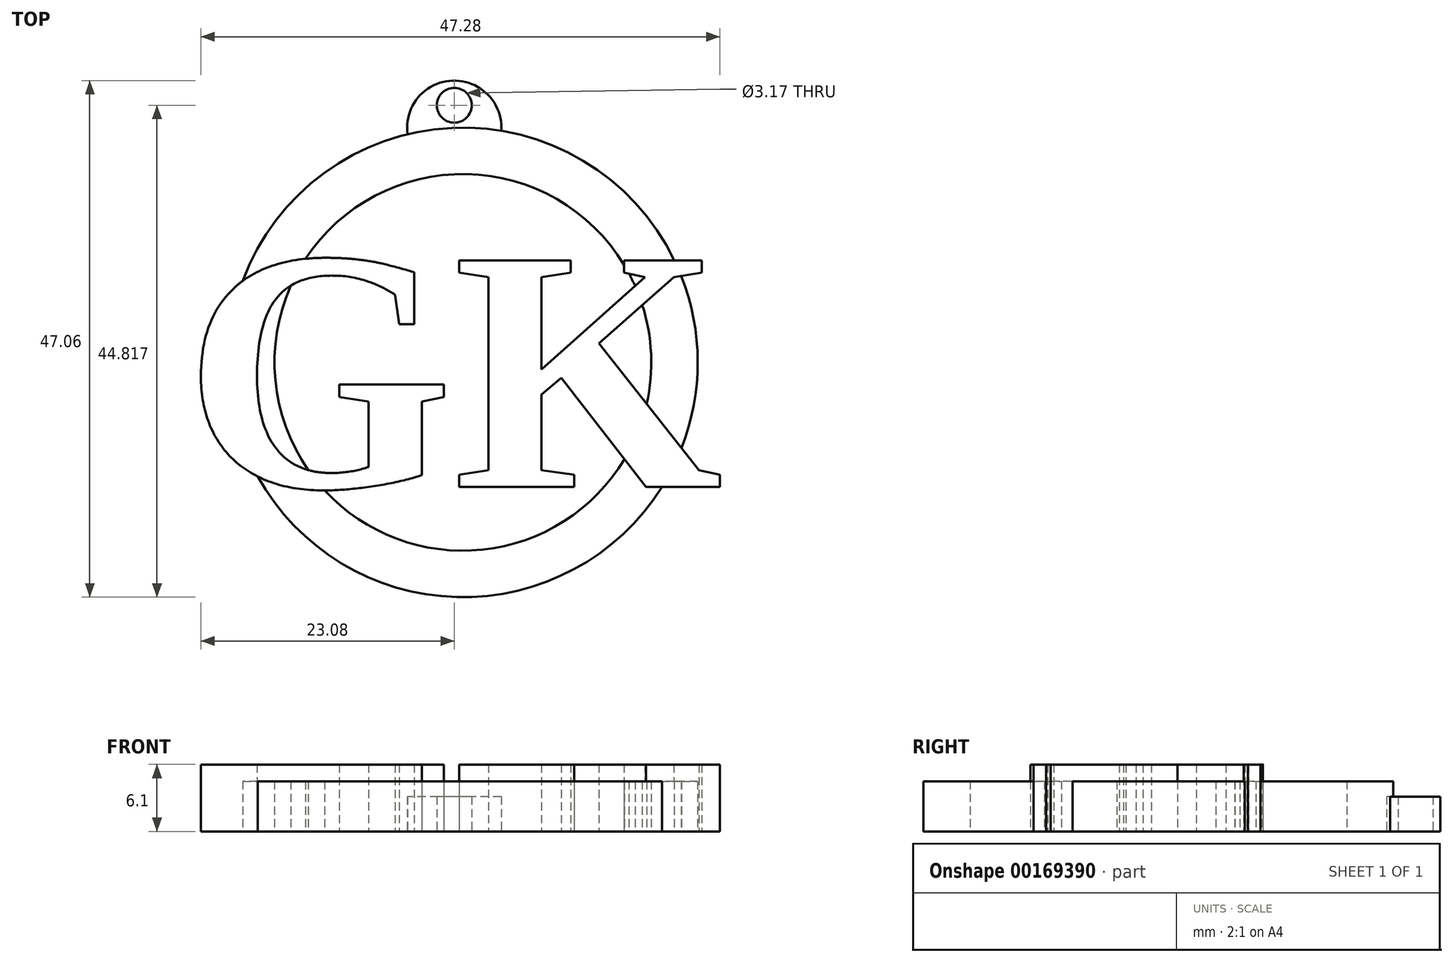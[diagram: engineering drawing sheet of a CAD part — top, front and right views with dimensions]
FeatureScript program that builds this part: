
annotation { "Feature Type Name" : "Feature", "Feature Type Description" : "" }
export const myFeature = defineFeature(function(context is Context, id is Id, definition is map)
    precondition{}
    {
        {
            var Q0;
            Q0=qCreatedBy(makeId("Top.planeOp"),FACE);
            var sketch = newSketch(context, id + "F0", { "sketchPlane" : qUnion([Q0])});
            skText(sketch, "E0", { "text": "GK", "fontName": "Tinos-Bold.ttf"});
            skCircle(sketch, "E1", {"center": v(0.78, 2.9) * mm, "radius": 17.16 * mm});
            skCircle(sketch, "E2", {"center": v(0.78, 2.9) * mm, "radius": 21.4 * mm});
            skCircle(sketch, "E3", {"center": v(0, 26.33) * mm, "radius": 1.59 * mm});
            skArc(sketch, "E4.trimOffspring", {"start": v(4.29, 24) * mm, "mid": v(-0.16, 28.57) * mm, "end": v(-4.26, 23.69) * mm});
            const initialGuessF0  = {"E0": [-0.02462, -0.00846, 1, 0, 0.02271]};
            skSetInitialGuess(sketch, initialGuessF0);
            skSolve(sketch);
        }
        {
            var Q0;
            {var subQ0=sQuery(id+"F0.wireOp",EDGE,"E0.sketch_text.stroke-35");Q0=makeQuery(id+"F0.imprint","IMPRINT",FACE,{"disambiguationData":[TD([[makeQuery(id+"F0.imprint","IMPRINT",EDGE,{"derivedFrom":subQ0}),-1.0]])]});}
            var Q1;
            {var subQ6=sQuery(id+"F0.wireOp",EDGE,"E0.sketch_text.stroke-29");var subQ8=sQuery(id+"F0.wireOp",EDGE,"E0.sketch_text.stroke-28");var subQ9=makeQuery(id+"F0.imprint","INTERSECT",VERTEX,{"derivedFrom":[subQ8,subQ6]});Q1=makeQuery(id+"F0.imprint","IMPRINT",FACE,{"disambiguationData":[TD([[makeQuery(id+"F0.imprint","IMPRINT",EDGE,{"disambiguationData":[TD([[subQ9,1.0]])],"derivedFrom":subQ8}),-1.0]])]});}
            var Q2;
            {var subQ0=sQuery(id+"F0.wireOp",EDGE,"E0.sketch_text.stroke-27");Q2=makeQuery(id+"F0.imprint","IMPRINT",FACE,{"disambiguationData":[TD([[makeQuery(id+"F0.imprint","IMPRINT",EDGE,{"derivedFrom":subQ0}),-1.0]])]});}
            var Q3;
            {var subQ1=sQuery(id+"F0.wireOp",EDGE,"E0.sketch_text.stroke-30");var subQ7=sQuery(id+"F0.wireOp",EDGE,"E2");var subQ8=makeQuery(id+"F0.imprint","INTERSECT",VERTEX,{"derivedFrom":[subQ1,subQ7]});Q3=makeQuery(id+"F0.imprint","IMPRINT",FACE,{"disambiguationData":[TD([[makeQuery(id+"F0.imprint","IMPRINT",EDGE,{"disambiguationData":[TD([[subQ8,1.0]])],"derivedFrom":subQ1}),-1.0]])]});}
            var Q4;
            {var subQ4=sQuery(id+"F0.wireOp",EDGE,"E0.sketch_text.stroke-31");Q4=makeQuery(id+"F0.imprint","IMPRINT",FACE,{"disambiguationData":[TD([[makeQuery(id+"F0.imprint","IMPRINT",EDGE,{"derivedFrom":subQ4}),-1.0]])]});}
            var Q5;
            {var subQ4=sQuery(id+"F0.wireOp",EDGE,"E0.sketch_text.stroke-7");Q5=makeQuery(id+"F0.imprint","IMPRINT",FACE,{"disambiguationData":[TD([[makeQuery(id+"F0.imprint","IMPRINT",EDGE,{"derivedFrom":subQ4}),-1.0]])]});}
            var Q6;
            {var subQ0=sQuery(id+"F0.wireOp",EDGE,"E0.sketch_text.stroke-0");Q6=makeQuery(id+"F0.imprint","IMPRINT",FACE,{"disambiguationData":[TD([[makeQuery(id+"F0.imprint","IMPRINT",EDGE,{"derivedFrom":subQ0}),-1.0]])]});}
            var Q7;
            {var subQ12=sQuery(id+"F0.wireOp",EDGE,"E0.sketch_text.stroke-2");Q7=makeQuery(id+"F0.imprint","IMPRINT",FACE,{"disambiguationData":[TD([[makeQuery(id+"F0.imprint","IMPRINT",EDGE,{"derivedFrom":subQ12}),-1.0]])]});}
            var Q8;
            {var subQ4=sQuery(id+"F0.wireOp",EDGE,"E0.sketch_text.stroke-4");Q8=makeQuery(id+"F0.imprint","IMPRINT",FACE,{"disambiguationData":[TD([[makeQuery(id+"F0.imprint","IMPRINT",EDGE,{"derivedFrom":subQ4}),-1.0]])]});}
            var Q9;
            {var subQ0=sQuery(id+"F0.wireOp",EDGE,"E0.sketch_text.stroke-51");var subQ1=sQuery(id+"F0.wireOp",EDGE,"E0.sketch_text.stroke-50");var subQ2=makeQuery(id+"F0.imprint","INTERSECT",VERTEX,{"derivedFrom":[subQ1,subQ0]});Q9=makeQuery(id+"F0.imprint","IMPRINT",FACE,{"disambiguationData":[TD([[makeQuery(id+"F0.imprint","IMPRINT",EDGE,{"disambiguationData":[TD([[subQ2,1.0]])],"derivedFrom":subQ1}),-1.0]])]});}
            extrude(context, id + "F1", {"entities" : qUnion([Q0, Q1, Q2, Q3, Q4, Q5, Q6, Q7, Q8, Q9]), "depth" : 6.1 * mm});
        }
        {
            var Q0;
            {var subQ1=sQuery(id+"F0.wireOp",EDGE,"E0.sketch_text.stroke-6");var subQ7=sQuery(id+"F0.wireOp",EDGE,"E2");var subQ9=makeQuery(id+"F0.imprint","INTERSECT",VERTEX,{"derivedFrom":[subQ1,subQ7]});Q0=makeQuery(id+"F0.imprint","IMPRINT",FACE,{"disambiguationData":[TD([[makeQuery(id+"F0.imprint","IMPRINT",EDGE,{"disambiguationData":[TD([[subQ9,-1.0]])],"derivedFrom":subQ1}),1.0]])]});}
            var Q1;
            {var subQ4=sQuery(id+"F0.wireOp",EDGE,"E0.sketch_text.stroke-16");Q1=makeQuery(id+"F0.imprint","IMPRINT",FACE,{"disambiguationData":[TD([[makeQuery(id+"F0.imprint","IMPRINT",EDGE,{"derivedFrom":subQ4}),1.0]])]});}
            var Q2;
            {var subQ6=sQuery(id+"F0.wireOp",EDGE,"E0.sketch_text.stroke-2");Q2=makeQuery(id+"F0.imprint","IMPRINT",FACE,{"disambiguationData":[TD([[makeQuery(id+"F0.imprint","IMPRINT",EDGE,{"derivedFrom":subQ6}),1.0]])]});}
            var Q3;
            {var subQ1=sQuery(id+"F0.wireOp",EDGE,"E0.sketch_text.stroke-29");var subQ7=sQuery(id+"F0.wireOp",EDGE,"E0.sketch_text.stroke-28");var subQ8=makeQuery(id+"F0.imprint","INTERSECT",VERTEX,{"derivedFrom":[subQ7,subQ1]});Q3=makeQuery(id+"F0.imprint","IMPRINT",FACE,{"disambiguationData":[TD([[makeQuery(id+"F0.imprint","IMPRINT",EDGE,{"disambiguationData":[TD([[subQ8,1.0]])],"derivedFrom":subQ7}),1.0]])]});}
            var Q4;
            {var subQ0=sQuery(id+"F0.wireOp",EDGE,"E0.sketch_text.stroke-50");var subQ1=sQuery(id+"F0.wireOp",EDGE,"E0.sketch_text.stroke-49");var subQ2=makeQuery(id+"F0.imprint","INTERSECT",VERTEX,{"derivedFrom":[subQ1,subQ0]});Q4=makeQuery(id+"F0.imprint","IMPRINT",FACE,{"disambiguationData":[TD([[makeQuery(id+"F0.imprint","IMPRINT",EDGE,{"disambiguationData":[TD([[subQ2,1.0]])],"derivedFrom":subQ1}),1.0]])]});}
            extrude(context, id + "F2", {"entities" : qUnion([Q0, Q1, Q2, Q3, Q4]), "operationType" : NewBodyOperationType.ADD, "depth" : 4.57 * mm});
        }
        {
            var Q0;
            Q0=makeQuery(id+"F0.imprint","IMPRINT",FACE,{"disambiguationData":[TD([[makeQuery(id+"F0.imprint","IMPRINT",EDGE,{"derivedFrom":sQuery(id+"F0.wireOp",EDGE,"E3")}),-1.0]])]});
            extrude(context, id + "F3", {"entities" : qUnion([Q0]), "operationType" : NewBodyOperationType.ADD, "depth" : 3.17 * mm});
        }
    });
